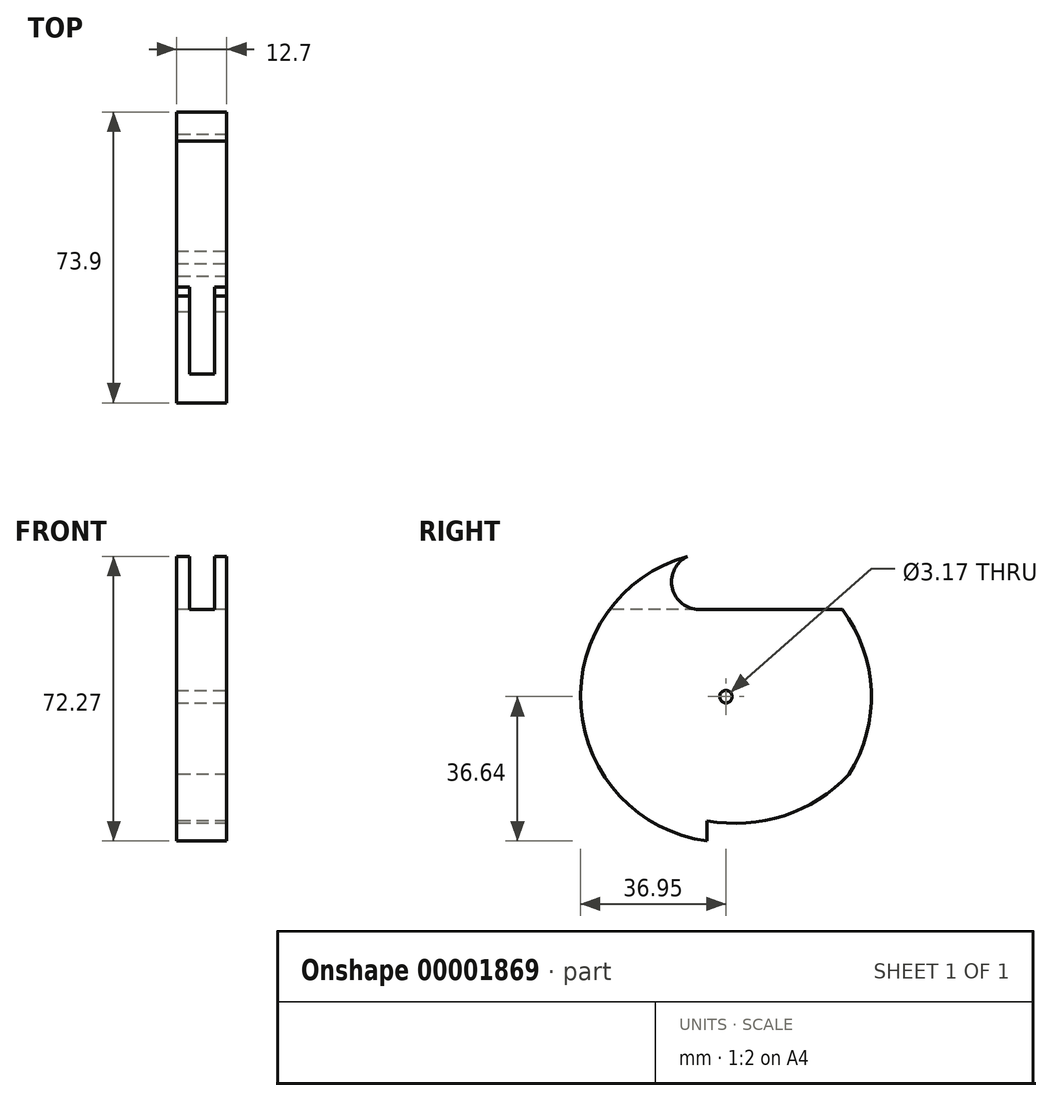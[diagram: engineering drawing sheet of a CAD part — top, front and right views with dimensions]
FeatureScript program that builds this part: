
annotation { "Feature Type Name" : "Feature", "Feature Type Description" : "" }
export const myFeature = defineFeature(function(context is Context, id is Id, definition is map)
    precondition{}
    {
        {
            var Q0;
            Q0=qCreatedBy(makeId("Right.planeOp"),FACE);
            var sketch = newSketch(context, id + "F0", { "sketchPlane" : qUnion([Q0])});
            skArc(sketch, "E0", {"start": v(31.21, -19.78) * mm, "mid": v(36.92, 1.46) * mm, "end": v(29.56, 22.18) * mm});
            skLineSegment(sketch, "E1", {"start": v(-4.77, -36.64) * mm, "end": v(-4.77, -31.52) * mm});
            skArc(sketch, "E2", {"start": v(-4.77, -31.52) * mm, "mid": v(14.72, -30.25) * mm, "end": v(31.21, -19.78) * mm});
            skPoint(sketch, "E3.end.orphan", {"position": v(0, 46.35) * mm});
            skPoint(sketch, "E3.start.orphan", {"position": v(0, 41.22) * mm});
            skArc(sketch, "E4", {"start": v(-9.8, 35.63) * mm, "mid": v(-13.7, 28.02) * mm, "end": v(-7.45, 22.18) * mm});
            skLineSegment(sketch, "E5", {"start": v(-7.45, 22.18) * mm, "end": v(29.56, 22.18) * mm});
            skArc(sketch, "E6.trimOffspring", {"start": v(-9.8, 35.63) * mm, "mid": v(-36.86, -2.56) * mm, "end": v(-4.77, -36.64) * mm});
            skPoint(sketch, "E7.orphan", {"position": v(-6.7, 36.34) * mm});
            skSolve(sketch);
        }
        {
            var Q0;
            Q0=makeQuery(id+"F0.imprint","IMPRINT",FACE,{"disambiguationData":[TD([[makeQuery(id+"F0.imprint","IMPRINT",EDGE,{"derivedFrom":sQuery(id+"F0.wireOp",EDGE,"E0")}),1.0]])]});
            extrude(context, id + "F1", {"entities" : qUnion([Q0]), "depth" : 12.7 * mm});
        }
        {
            var Q0;
            Q0=makeQuery(id+"F1.opExtrude","SWEPT_FACE",FACE,{"disambiguationData":[OSD([sQuery(id+"F0.wireOp",EDGE,"E5")])]});
            var sketch = newSketch(context, id + "F2", { "sketchPlane" : qUnion([Q0])});
            skLineSegment(sketch, "E8", {"start": v(0, 37.22) * mm, "end": v(0, -38.08) * mm});
            skLineSegment(sketch, "E9", {"start": v(3.24, 37.22) * mm, "end": v(9.6, 37.22) * mm});
            skLineSegment(sketch, "E10.0", {"start": v(9.6, 37.22) * mm, "end": v(9.6, -38.65) * mm});
            skLineSegment(sketch, "E11.0.MirrorCS", {"start": v(3.24, 37.22) * mm, "end": v(3.24, -38.65) * mm});
            skPoint(sketch, "E12.start.orphan", {"position": v(6.42, 37.22) * mm});
            skPoint(sketch, "E13.orphan", {"position": v(12.84, 37.22) * mm});
            skLineSegment(sketch, "E14", {"start": v(3.24, -38.65) * mm, "end": v(9.6, -38.65) * mm});
            skSolve(sketch);
        }
        {
            var Q0;
            {var subQ5=sQuery(id+"F2.wireOp",EDGE,"E14");Q0=makeQuery(id+"F2.imprint","IMPRINT",FACE,{"disambiguationData":[TD([[makeQuery(id+"F2.imprint","IMPRINT",EDGE,{"derivedFrom":subQ5}),1.0]])]});}
            extrude(context, id + "F3", {"entities" : qUnion([Q0]), "operationType" : NewBodyOperationType.REMOVE, "depth" : 25.4 * mm});
        }
        {
            var Q0;
            Q0=makeQuery(id+"F1.opExtrude","CAP_FACE",FACE,{"disambiguationData":[OSD([sQuery(id+"F0.wireOp",EDGE,"E0"),sQuery(id+"F0.wireOp",EDGE,"E1"),sQuery(id+"F0.wireOp",EDGE,"E2"),sQuery(id+"F0.wireOp",EDGE,"E4"),sQuery(id+"F0.wireOp",EDGE,"E5"),sQuery(id+"F0.wireOp",EDGE,"E6.trimOffspring")])],"isStart":false});
            var sketch = newSketch(context, id + "F4", { "sketchPlane" : qUnion([Q0])});
            skCircle(sketch, "E15", {"center": v(0, 0) * mm, "radius": 1.59 * mm});
            skSolve(sketch);
        }
        {
            var Q0;
            Q0=makeQuery(id+"F4.imprint","IMPRINT",FACE,{"disambiguationData":[TD([[makeQuery(id+"F4.imprint","IMPRINT",EDGE,{"derivedFrom":sQuery(id+"F4.wireOp",EDGE,"E15")}),1.0]])]});
            extrude(context, id + "F5", {"entities" : qUnion([Q0]), "operationType" : NewBodyOperationType.REMOVE, "oppositeDirection" : true, "depth" : 25.4 * mm});
        }
    });
